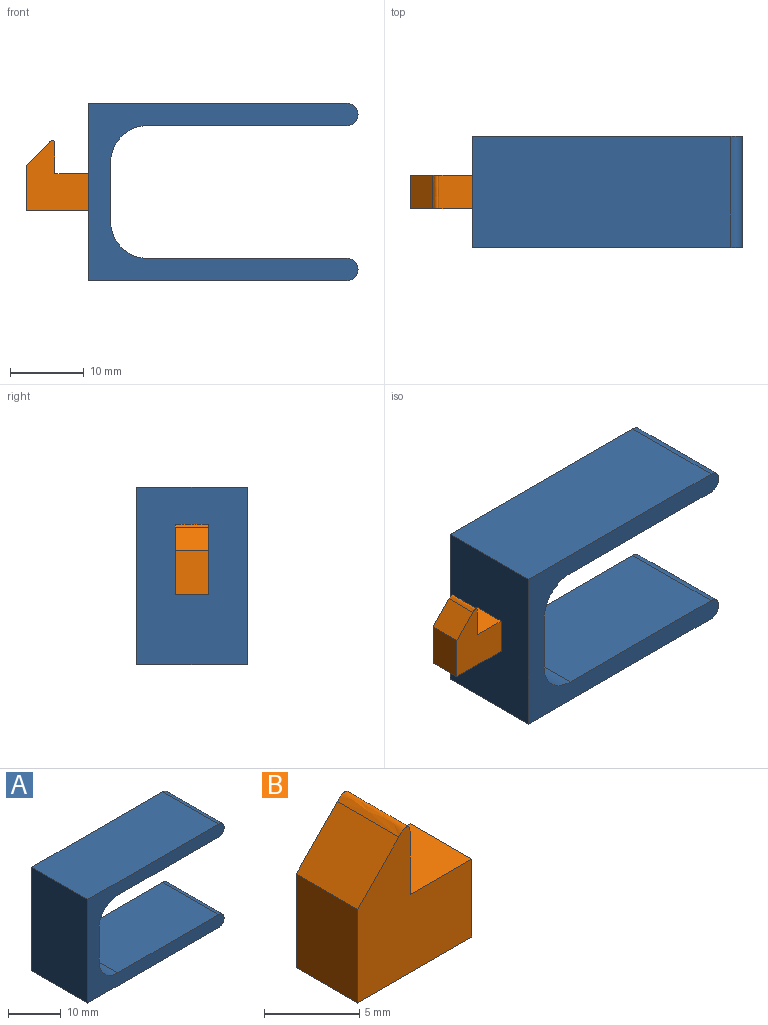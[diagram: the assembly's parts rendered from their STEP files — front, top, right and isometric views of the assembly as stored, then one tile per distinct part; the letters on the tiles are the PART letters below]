
ASSEMBLY  parts=2 mates=1
PART A: 12 faces, bbox 36.5x15x24 mm
  f0: cylinder r=1.5mm len=15mm, axis (0,1,0), area 70.7mm2, adj f1,f9,f10,f11
  f1: plane 35x15mm, normal (0,0,1), area 525mm2, adj f0,f2,f10,f11
  f2: plane 24x15mm, normal (-1,0,0), area 360mm2, adj f1,f3,f10,f11
  f3: plane 35x15mm, normal (0,0,-1), area 525mm2, adj f2,f4,f10,f11
  f4: cylinder r=1.5mm len=15mm, axis (0,1,0), area 70.7mm2, adj f3,f5,f10,f11
  f5: plane 27x15mm, normal (0,0,1), area 405mm2, adj f4,f6,f10,f11
  f6: cylinder r=5mm len=15mm, axis (0,1,0), area 117.8mm2, adj f5,f7,f10,f11
  f7: plane 15x8mm, normal (1,0,0), area 120mm2, adj f6,f8,f10,f11
  f8: cylinder r=5mm len=15mm, axis (0,1,0), area 117.8mm2, adj f7,f9,f10,f11
  f9: plane 27x15mm, normal (0,0,-1), area 405mm2, adj f0,f8,f10,f11
  f10: plane 36.5x24mm, normal (0,-1,0), area 281.8mm2, adj f0,f1,f2,f3,f4,f5,f6,f7
  f11: plane 36.5x24mm, normal (0,1,0), area 281.8mm2, adj f0,f1,f2,f3,f4,f5,f6,f7
PART B: 9 faces, bbox 8.5x5x10 mm
  f0: plane 8.47x4.55mm, normal (0,0,-1), area 38.5mm2, adj f1,f5,f6,f7
  f1: plane 5x4.55mm, normal (1,0,0), area 22.8mm2, adj f0,f2,f6,f7
  f2: plane 4.55x4.55mm, normal (0,0,1), area 20.7mm2, adj f1,f3,f6,f7
  f3: plane 4.55x3.78mm, normal (1,0,0), area 17.2mm2, adj f2,f6,f7,f8
  f4: plane 4.55x3.13mm, normal (-0.71,0,0.7), area 19.9mm2, adj f5,f6,f7,f8
  f5: plane 6x4.55mm, normal (-1,0,0), area 27.3mm2, adj f0,f4,f6,f7
  f6: plane 9.69x8.47mm, normal (0,-1,0), area 53.9mm2, adj f0,f1,f2,f3,f4,f5,f8
  f7: plane 9.69x8.47mm, normal (0,1,0), area 53.9mm2, adj f0,f1,f2,f3,f4,f5,f8
  f8: bspline ~5.01x1.22mm, area 7mm2, adj f3,f4,f6,f7
PLACE A t=(4.84,-11.6,3.78)mm
PLACE B t=(3.36,-16.83,10.44)mm
MATE fastened B.f1 <-> A.f2  axis (1,0,0) through (-55.17,-19.1,3.17)mm
